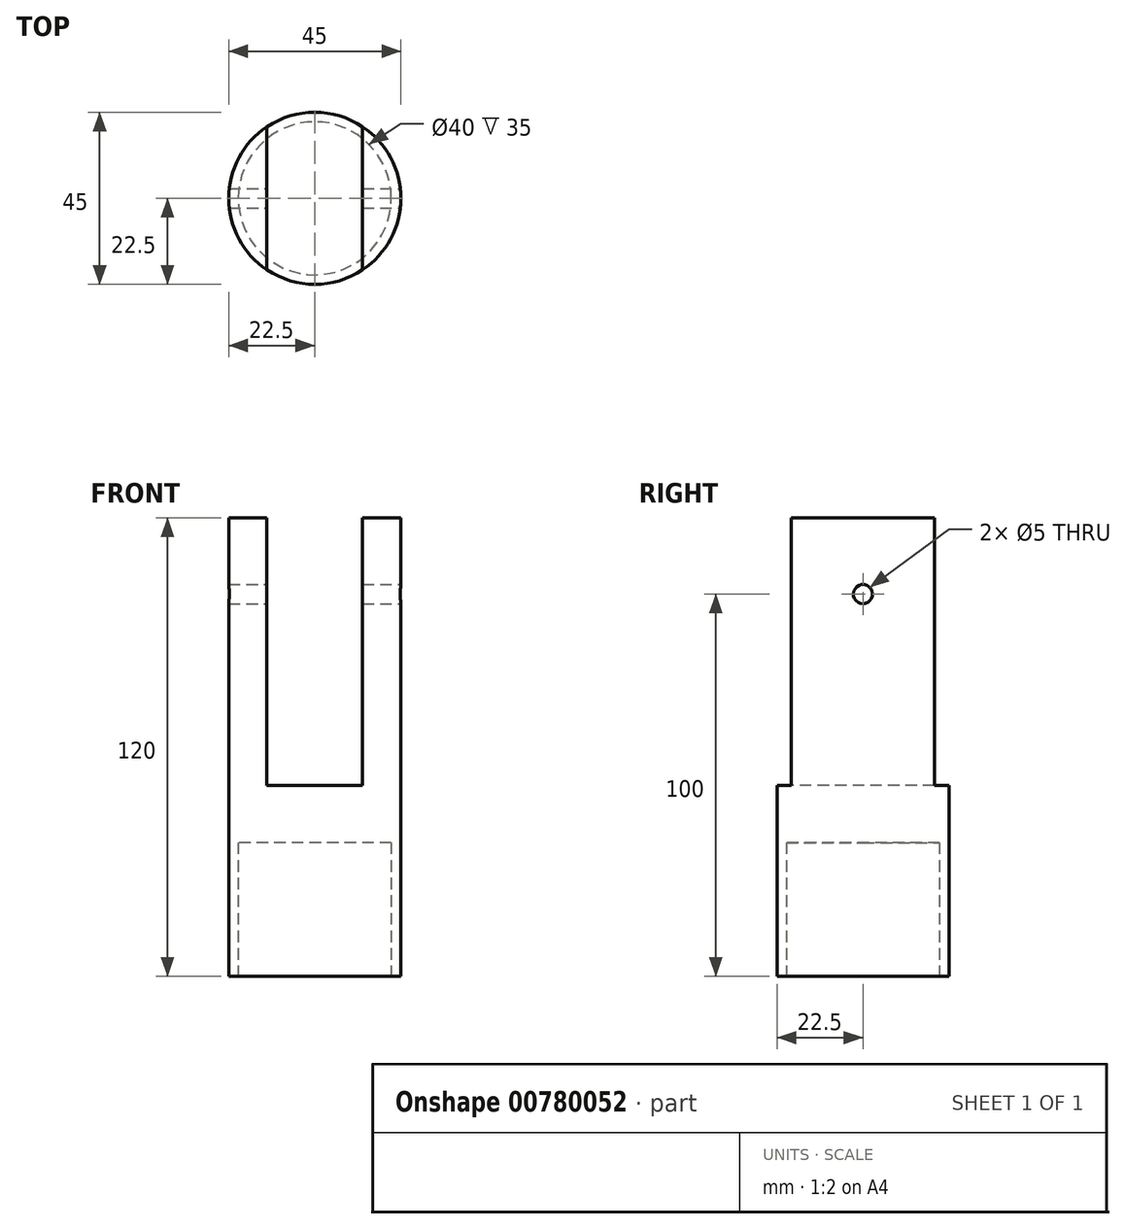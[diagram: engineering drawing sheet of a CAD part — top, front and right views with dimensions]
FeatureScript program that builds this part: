
annotation { "Feature Type Name" : "Feature", "Feature Type Description" : "" }
export const myFeature = defineFeature(function(context is Context, id is Id, definition is map)
    precondition{}
    {
        {
            var Q0;
            Q0=qCreatedBy(makeId("Top.planeOp"),FACE);
            var sketch = newSketch(context, id + "F0", { "sketchPlane" : qUnion([Q0])});
            skCircle(sketch, "E0", {"center": v(0, 0) * mm, "radius": 22.5 * mm});
            skSolve(sketch);
        }
        {
            var Q0;
            Q0=makeQuery(id+"F0.imprint","IMPRINT",FACE,{"disambiguationData":[TD([[makeQuery(id+"F0.imprint","IMPRINT",EDGE,{"derivedFrom":sQuery(id+"F0.wireOp",EDGE,"E0")}),1.0]])]});
            extrude(context, id + "F1", {"entities" : qUnion([Q0]), "depth" : 120 * mm, "offsetDistance" : 25 * mm});
        }
        {
            var Q0;
            Q0=makeQuery(id+"F1.opExtrude","CAP_FACE",FACE,{"disambiguationData":[OSD([sQuery(id+"F0.wireOp",EDGE,"E0")])],"isStart":false});
            var sketch = newSketch(context, id + "F2", { "sketchPlane" : qUnion([Q0])});
            skLineSegment(sketch, "E1", {"start": v(-12.5, 18.7) * mm, "end": v(-12.5, -18.7) * mm});
            skLineSegment(sketch, "E2", {"start": v(12.5, 18.7) * mm, "end": v(12.5, -18.7) * mm});
            skSolve(sketch);
        }
        {
            var Q0;
            {var subQ0=sQuery(id+"F2.wireOp",EDGE,"E1");Q0=makeQuery(id+"F2.imprint","IMPRINT",FACE,{"disambiguationData":[TD([[makeQuery(id+"F2.imprint","IMPRINT",EDGE,{"derivedFrom":subQ0}),1.0]])]});}
            extrude(context, id + "F3", {"entities" : qUnion([Q0]), "operationType" : NewBodyOperationType.REMOVE, "oppositeDirection" : true, "depth" : 70 * mm, "offsetDistance" : 25 * mm});
        }
        {
            var Q0;
            Q0=makeQuery(id+"F0.imprint","IMPRINT",FACE,{"disambiguationData":[TD([[makeQuery(id+"F0.imprint","IMPRINT",EDGE,{"derivedFrom":sQuery(id+"F0.wireOp",EDGE,"E0")}),1.0]])]});
            var sketch = newSketch(context, id + "F4", { "sketchPlane" : qUnion([Q0])});
            skCircle(sketch, "E3", {"center": v(0, 0) * mm, "radius": 20 * mm});
            skSolve(sketch);
        }
        {
            var Q0;
            Q0 = qSketchRegion(id + "F4", true);
            extrude(context, id + "F5", {"entities" : qUnion([Q0]), "operationType" : NewBodyOperationType.REMOVE, "depth" : 35 * mm, "offsetDistance" : 25 * mm});
        }
        {
            var Q0;
            Q0=qCreatedBy(makeId("Right.planeOp"),FACE);
            cPlane(context, id + "F6", {"entities" : qUnion([Q0]), "cplaneType" : CPlaneType.OFFSET, "offset" : 22.5 * mm, "width" : 150 * mm, "height" : 150 * mm});
        }
        {
            var Q0;
            Q0=qCreatedBy(id+"F6.planeOp",FACE);
            var sketch = newSketch(context, id + "F7", { "sketchPlane" : qUnion([Q0])});
            skLineSegment(sketch, "E4", {"start": v(-18.7, 100) * mm, "end": v(18.7, 100) * mm});
            skPoint(sketch, "E5", {"position": v(0, 100) * mm});
            skSolve(sketch);
        }
        {
            var Q0;
            Q0=sQuery(id+"F7.wireOp",VERTEX,"E5");
            var Q1;
            Q1=makeQuery(id+"F1.opExtrude","SWEPT_BODY",BODY,{"disambiguationData":[OSD([sQuery(id+"F0.wireOp",EDGE,"E0")])]});
            hole(context, id + "F8", {"style" : HoleStyle.SIMPLE, "endStyle" : HoleEndStyle.THROUGH, "holeDiameter" : 5 * mm, "majorDiameter" : 5 * mm, "isTappedThrough" : true, "tappedDepth" : 12 * mm, "tapClearance" : 3, "locations" : qUnion([Q0]), "scope" : qUnion([Q1])});
        }
    });
